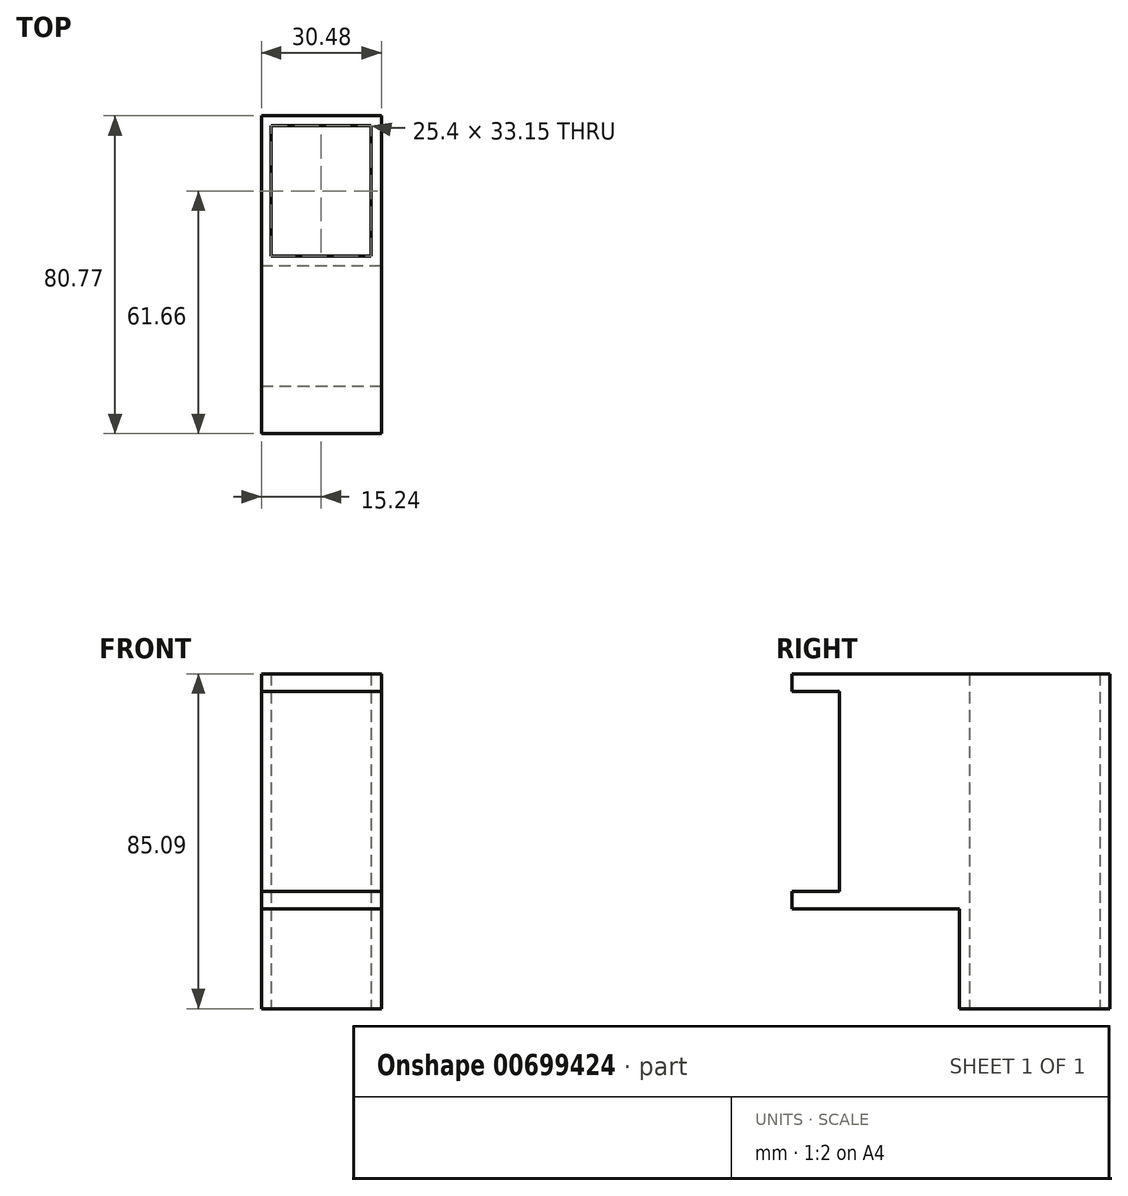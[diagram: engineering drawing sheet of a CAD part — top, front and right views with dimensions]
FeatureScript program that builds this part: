
annotation { "Feature Type Name" : "Feature", "Feature Type Description" : "" }
export const myFeature = defineFeature(function(context is Context, id is Id, definition is map)
    precondition{}
    {
        {
            var Q0;
            Q0=qCreatedBy(makeId("Top.planeOp"),FACE);
            var sketch = newSketch(context, id + "F0", { "sketchPlane" : qUnion([Q0])});
            skLineSegment(sketch, "E0.bottom", {"start": v(15.24, -19.11) * mm, "end": v(-15.24, -19.11) * mm});
            skLineSegment(sketch, "E0.top", {"start": v(15.24, 19.11) * mm, "end": v(-15.24, 19.11) * mm});
            skLineSegment(sketch, "E0.left", {"start": v(15.24, -19.11) * mm, "end": v(15.24, 19.11) * mm});
            skLineSegment(sketch, "E0.right", {"start": v(-15.24, -19.11) * mm, "end": v(-15.24, 19.11) * mm});
            skPoint(sketch, "E0.middle", {"position": v(0, 0) * mm});
            skSolve(sketch);
        }
        {
            var Q0;
            Q0=makeQuery(id+"F0.imprint","IMPRINT",FACE,{"disambiguationData":[TD([[makeQuery(id+"F0.imprint","IMPRINT",EDGE,{"derivedFrom":sQuery(id+"F0.wireOp",EDGE,"E0.bottom")}),-1.0]])]});
            var sketch = newSketch(context, id + "F1", { "sketchPlane" : qUnion([Q0])});
            skLineSegment(sketch, "E1.bottom", {"start": v(12.7, -16.57) * mm, "end": v(-12.7, -16.57) * mm});
            skLineSegment(sketch, "E1.top", {"start": v(12.7, 16.57) * mm, "end": v(-12.7, 16.57) * mm});
            skLineSegment(sketch, "E1.left", {"start": v(12.7, -16.57) * mm, "end": v(12.7, 16.57) * mm});
            skLineSegment(sketch, "E1.right", {"start": v(-12.7, -16.57) * mm, "end": v(-12.7, 16.57) * mm});
            skPoint(sketch, "E1.middle", {"position": v(0, 0) * mm});
            skSolve(sketch);
        }
        {
            var Q0;
            Q0=makeQuery(id+"F1.imprint","IMPRINT",FACE,{"disambiguationData":[TD([[makeQuery(id+"F1.imprint","IMPRINT",EDGE,{"derivedFrom":sQuery(id+"F1.wireOp",EDGE,"E1.bottom")}),1.0]])]});
            extrude(context, id + "F2", {"entities" : qUnion([Q0]), "depth" : 66.04 * mm, "offsetDistance" : 25.4 * mm});
        }
        {
            var Q0;
            Q0=makeQuery(id+"F2.opExtrude","SWEPT_FACE",FACE,{"disambiguationData":[OSD([sQuery(id+"F0.wireOp",EDGE,"E0.bottom")])]});
            var sketch = newSketch(context, id + "F3", { "sketchPlane" : qUnion([Q0])});
            skLineSegment(sketch, "E2.bottom", {"start": v(-15.24, 61.6) * mm, "end": v(15.24, 61.6) * mm});
            skLineSegment(sketch, "E2.top", {"start": v(-15.24, 10.8) * mm, "end": v(15.24, 10.8) * mm});
            skLineSegment(sketch, "E2.left", {"start": v(-15.24, 61.6) * mm, "end": v(-15.24, 10.8) * mm});
            skLineSegment(sketch, "E2.right", {"start": v(15.24, 61.6) * mm, "end": v(15.24, 10.8) * mm});
            skSolve(sketch);
        }
        {
            var Q0;
            Q0=makeQuery(id+"F3.imprint","IMPRINT",FACE,{"disambiguationData":[TD([[makeQuery(id+"F3.imprint","IMPRINT",EDGE,{"derivedFrom":sQuery(id+"F3.wireOp",EDGE,"E2.bottom")}),-1.0]])]});
            extrude(context, id + "F4", {"entities" : qUnion([Q0]), "operationType" : NewBodyOperationType.ADD, "depth" : 30.48 * mm, "offsetDistance" : 25.4 * mm});
        }
        {
            var Q0;
            {var subQ2=sQuery(id+"F0.wireOp",EDGE,"E0.bottom");Q0=makeQuery(id+"F4.boolean.opBoolean","SPLIT",FACE,{"disambiguationData":[TD([makeQuery(id+"F4.opExtrude","SWEPT_FACE",FACE,{"disambiguationData":[OSD([sQuery(id+"F3.wireOp",EDGE,"E2.bottom")])]})])],"derivedFrom":makeQuery(id+"F2.opExtrude","SWEPT_FACE",FACE,{"disambiguationData":[OSD([subQ2])]})});}
            extrude(context, id + "F5", {"entities" : qUnion([Q0]), "operationType" : NewBodyOperationType.ADD, "depth" : 42.55 * mm, "offsetDistance" : 25.4 * mm});
        }
        {
            var Q0;
            {var subQ2=sQuery(id+"F0.wireOp",EDGE,"E0.bottom");Q0=makeQuery(id+"F4.boolean.opBoolean","SPLIT",FACE,{"disambiguationData":[TD([makeQuery(id+"F4.opExtrude","SWEPT_FACE",FACE,{"disambiguationData":[OSD([sQuery(id+"F3.wireOp",EDGE,"E2.top")])]})])],"derivedFrom":makeQuery(id+"F2.opExtrude","SWEPT_FACE",FACE,{"disambiguationData":[OSD([subQ2])]})});}
            var sketch = newSketch(context, id + "F6", { "sketchPlane" : qUnion([Q0])});
            skLineSegment(sketch, "E3.bottom", {"start": v(-15.24, 10.8) * mm, "end": v(15.24, 10.8) * mm});
            skLineSegment(sketch, "E3.top", {"start": v(-15.24, 6.36) * mm, "end": v(15.24, 6.36) * mm});
            skLineSegment(sketch, "E3.left", {"start": v(-15.24, 10.8) * mm, "end": v(-15.24, 6.36) * mm});
            skLineSegment(sketch, "E3.right", {"start": v(15.24, 10.8) * mm, "end": v(15.24, 6.36) * mm});
            skSolve(sketch);
        }
        {
            var Q0;
            Q0 = qSketchRegion(id + "F6", true);
            extrude(context, id + "F7", {"entities" : qUnion([Q0]), "operationType" : NewBodyOperationType.ADD, "depth" : 42.55 * mm, "offsetDistance" : 25.4 * mm});
        }
        {
            var Q0;
            Q0=makeQuery(id+"F0.imprint","IMPRINT",FACE,{"disambiguationData":[TD([[makeQuery(id+"F0.imprint","IMPRINT",EDGE,{"derivedFrom":sQuery(id+"F0.wireOp",EDGE,"E0.bottom")}),-1.0]])]});
            extrude(context, id + "F8", {"entities" : qUnion([Q0]), "operationType" : NewBodyOperationType.ADD, "oppositeDirection" : true, "depth" : 19.05 * mm, "offsetDistance" : 25.4 * mm});
        }
        {
            var Q0;
            Q0=makeQuery(id+"F8.opExtrude","CAP_FACE",FACE,{"disambiguationData":[OSD([sQuery(id+"F0.wireOp",EDGE,"E0.bottom"),sQuery(id+"F0.wireOp",EDGE,"E0.top"),sQuery(id+"F0.wireOp",EDGE,"E0.left"),sQuery(id+"F0.wireOp",EDGE,"E0.right")])],"isStart":true});
            extrude(context, id + "F9", {"entities" : qUnion([Q0]), "operationType" : NewBodyOperationType.REMOVE, "oppositeDirection" : true, "depth" : 25.4 * mm, "offsetDistance" : 25.4 * mm});
        }
    });
